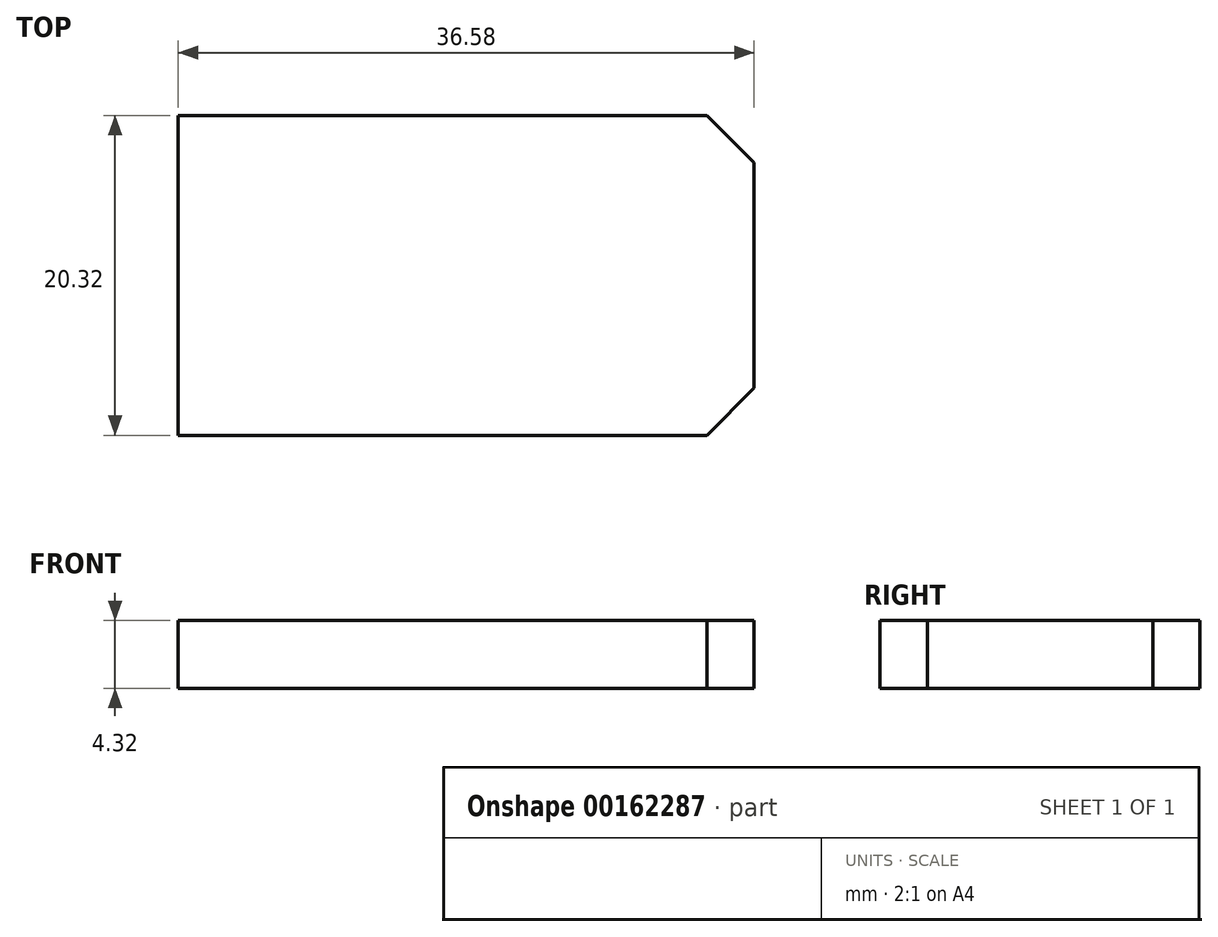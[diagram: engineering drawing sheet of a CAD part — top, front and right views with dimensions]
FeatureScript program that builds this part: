
annotation { "Feature Type Name" : "Feature", "Feature Type Description" : "" }
export const myFeature = defineFeature(function(context is Context, id is Id, definition is map)
    precondition{}
    {
        {
            var Q0;
            Q0=qCreatedBy(makeId("Top.planeOp"),FACE);
            var sketch = newSketch(context, id + "F0", { "sketchPlane" : qUnion([Q0])});
            skLineSegment(sketch, "E0.bottom", {"start": v(-20.71, 10.25) * mm, "end": v(15.87, 10.25) * mm});
            skLineSegment(sketch, "E0.top", {"start": v(-20.71, -10.07) * mm, "end": v(15.87, -10.07) * mm});
            skLineSegment(sketch, "E0.left", {"start": v(-20.71, 10.25) * mm, "end": v(-20.71, -10.07) * mm});
            skLineSegment(sketch, "E0.right", {"start": v(15.87, 10.25) * mm, "end": v(15.87, -10.07) * mm});
            skSolve(sketch);
        }
        {
            var Q0;
            Q0=makeQuery(id+"F0.imprint","IMPRINT",FACE,{"disambiguationData":[TD([[makeQuery(id+"F0.imprint","IMPRINT",EDGE,{"derivedFrom":sQuery(id+"F0.wireOp",EDGE,"E0.bottom")}),-1.0]])]});
            extrude(context, id + "F1", {"entities" : qUnion([Q0]), "depth" : 4.32 * mm});
        }
        {
            var Q0;
            Q0=makeQuery(id+"F1.opExtrude","SWEPT_EDGE",EDGE,{"disambiguationData":[OSD([sQuery(id+"F0.wireOp",EDGE,"E0.bottom"),sQuery(id+"F0.wireOp",EDGE,"E0.right")])]});
            var Q1;
            Q1=makeQuery(id+"F1.opExtrude","SWEPT_EDGE",EDGE,{"disambiguationData":[OSD([sQuery(id+"F0.wireOp",EDGE,"E0.top"),sQuery(id+"F0.wireOp",EDGE,"E0.right")])]});
            chamfer(context, id + "F2", {"entities" : qUnion([Q0, Q1]), "width" : 3 * mm, "tangentPropagation" : true});
        }
    });
